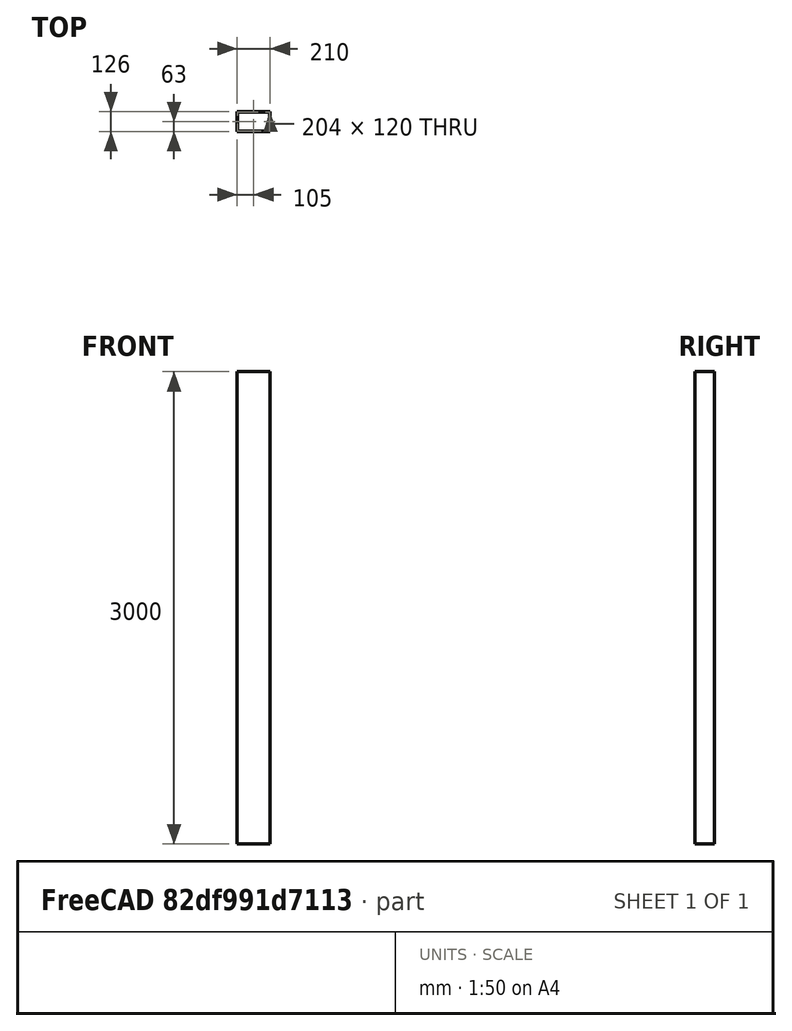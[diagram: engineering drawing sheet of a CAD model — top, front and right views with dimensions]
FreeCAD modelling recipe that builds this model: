
FCSTD DOCUMENT  (FreeCAD 0.21R33771 (Git))
Label: PQ4
License: All rights reserved
LicenseURL: https://en.wikipedia.org/wiki/All_rights_reserved
objects: Sketcher::SketchObject×1, PartDesign::Pad×1, PartDesign::Body×1
note: 4 computed .brp shape members not serialized (recipe doc carries the construction recipe); baked Part::Feature solids carry a one-line shape summary decoded from their .brp

FEATURE [Sketcher::SketchObject] Sketch
  FullyConstrained = true
  MapMode = 5
  Support = -> [XY_Plane]
  sketch-geometry (10):
    g0: LineSegment StartX=-102 StartY=-60 StartZ=0 EndX=-102 EndY=60 EndZ=0
    g1: LineSegment StartX=-102 StartY=60 StartZ=0 EndX=102 EndY=60 EndZ=0
    g2: LineSegment StartX=102 StartY=60 StartZ=0 EndX=102 EndY=-60 EndZ=0
    g3: LineSegment StartX=102 StartY=-60 StartZ=0 EndX=-102 EndY=-60 EndZ=0
    g4: GeomPoint X=0 Y=0 Z=0
    g5: LineSegment StartX=-105 StartY=-63 StartZ=0 EndX=-105 EndY=63 EndZ=0
    g6: LineSegment StartX=-105 StartY=63 StartZ=0 EndX=105 EndY=63 EndZ=0
    g7: LineSegment StartX=105 StartY=63 StartZ=0 EndX=105 EndY=-63 EndZ=0
    g8: LineSegment StartX=105 StartY=-63 StartZ=0 EndX=-105 EndY=-63 EndZ=0
    g9: GeomPoint X=0 Y=0 Z=0
  constraints (24):
    c: Coincident(g0,g1)
    c: Coincident(g1,g2)
    c: Coincident(g2,g3)
    c: Coincident(g3,g0)
    c: Horizontal(g1)
    c: Horizontal(g3)
    c: Vertical(g0)
    c: Vertical(g2)
    c: Symmetric(g1,g0,g4)
    c: Coincident(g4,g-1)
    c: Coincident(g5,g6)
    c: Coincident(g6,g7)
    c: Coincident(g7,g8)
    c: Coincident(g8,g5)
    c: Horizontal(g6)
    c: Horizontal(g8)
    c: Vertical(g5)
    c: Vertical(g7)
    c: Symmetric(g6,g5,g9)
    c: Coincident(g9,g4)
    c: DistanceX(g1,g1) = 204
    c: DistanceX(g6,g6) = 210
    c: DistanceY(g2,g2) = 120
    c: DistanceY(g7,g7) = 126
FEATURE [PartDesign::Pad] Pad
  Direction = (0,0,1)
  Length = 3000
  Length2 = 10
  Midplane = true
  Profile = -> Sketch
  ReferenceAxis = -> Sketch [N_Axis]
  Type = 0
FEATURE [PartDesign::Body] Body
  Group = -> [Sketch,Pad]
  Origin = -> Origin
  Tip = -> Pad
